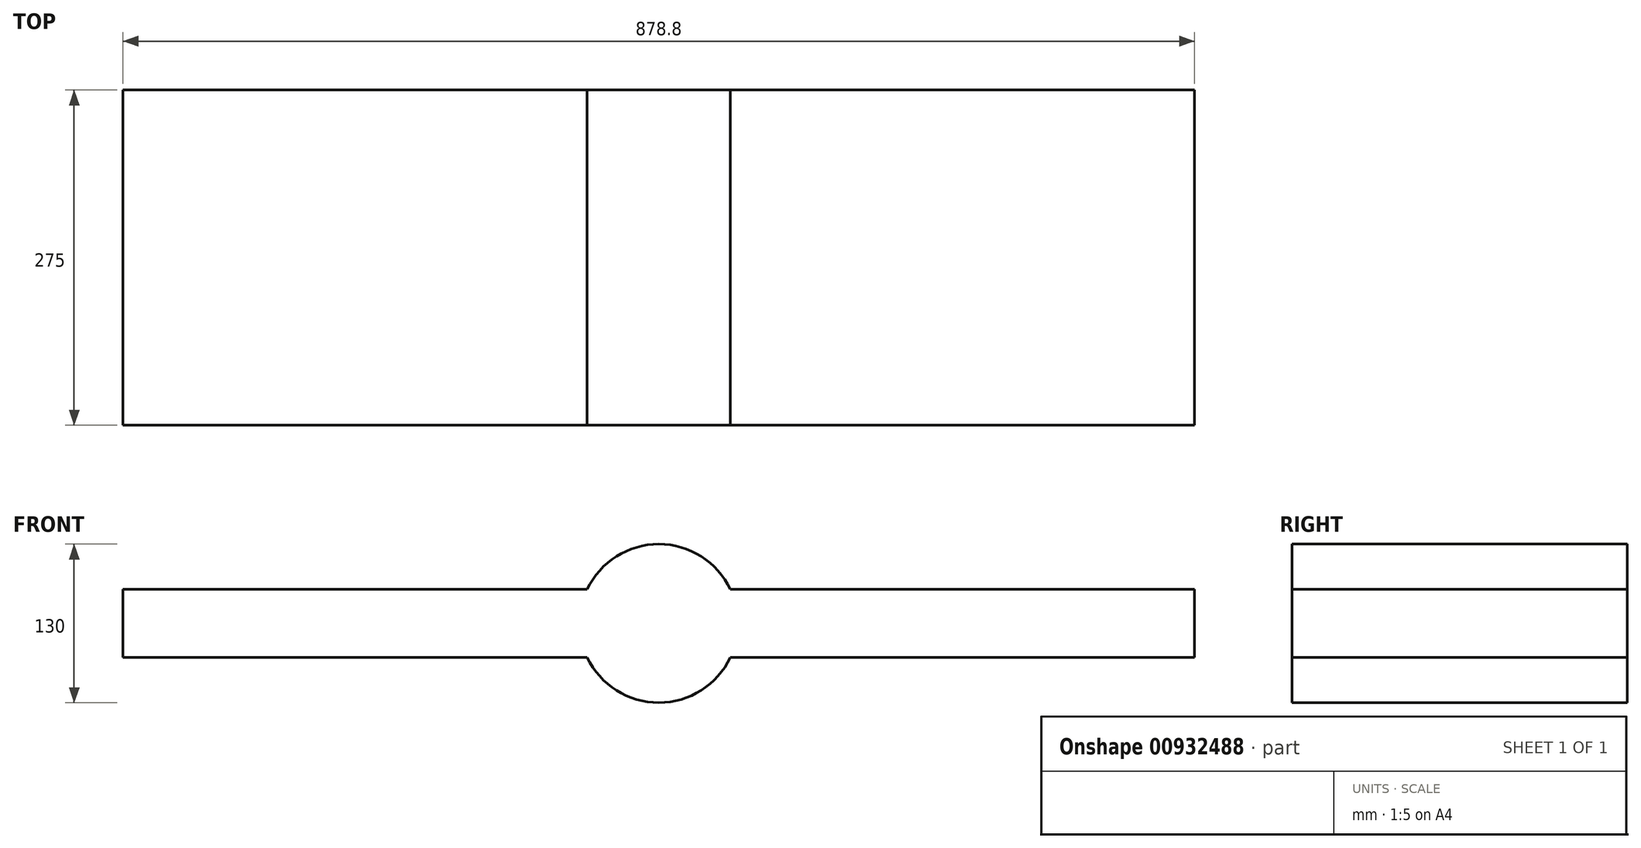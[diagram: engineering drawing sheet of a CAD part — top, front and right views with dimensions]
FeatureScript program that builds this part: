
annotation { "Feature Type Name" : "Feature", "Feature Type Description" : "" }
export const myFeature = defineFeature(function(context is Context, id is Id, definition is map)
    precondition{}
    {
        {
            var Q0;
            Q0=qCreatedBy(makeId("Front.planeOp"),FACE);
            var sketch = newSketch(context, id + "F0", { "sketchPlane" : qUnion([Q0])});
            skCircle(sketch, "E0", {"center": v(0, 0) * mm, "radius": 65 * mm});
            skLineSegment(sketch, "E1", {"start": v(0, 0) * mm, "end": v(-65, 0) * mm});
            skLineSegment(sketch, "E2", {"start": v(0, 65) * mm, "end": v(0, 0) * mm});
            skLineSegment(sketch, "E3", {"start": v(65, 0) * mm, "end": v(0, 0) * mm});
            skLineSegment(sketch, "E4", {"start": v(0, -65) * mm, "end": v(0, 0) * mm});
            skLineSegment(sketch, "E5.bottom", {"start": v(439.4, 27.92) * mm, "end": v(-439.4, 27.92) * mm});
            skLineSegment(sketch, "E5.top", {"start": v(439.4, -27.92) * mm, "end": v(-439.4, -27.92) * mm});
            skLineSegment(sketch, "E5.left", {"start": v(439.4, 27.92) * mm, "end": v(439.4, -27.92) * mm});
            skLineSegment(sketch, "E5.right", {"start": v(-439.4, 27.92) * mm, "end": v(-439.4, -27.92) * mm});
            skSolve(sketch);
        }
        {
            var Q0;
            {var subQ0=sQuery(id+"F0.wireOp",EDGE,"E5.right");Q0=makeQuery(id+"F0.imprint","IMPRINT",FACE,{"disambiguationData":[TD([[makeQuery(id+"F0.imprint","IMPRINT",EDGE,{"derivedFrom":subQ0}),1.0]])]});}
            var Q1;
            {var subQ0=sQuery(id+"F0.wireOp",EDGE,"E5.left");Q1=makeQuery(id+"F0.imprint","IMPRINT",FACE,{"disambiguationData":[TD([[makeQuery(id+"F0.imprint","IMPRINT",EDGE,{"derivedFrom":subQ0}),-1.0]])]});}
            var Q2;
            {var subQ0=sQuery(id+"F0.wireOp",EDGE,"E1");Q2=makeQuery(id+"F0.imprint","IMPRINT",FACE,{"disambiguationData":[TD([[makeQuery(id+"F0.imprint","IMPRINT",EDGE,{"derivedFrom":subQ0}),-1.0]])]});}
            var Q3;
            {var subQ0=sQuery(id+"F0.wireOp",EDGE,"E3");Q3=makeQuery(id+"F0.imprint","IMPRINT",FACE,{"disambiguationData":[TD([[makeQuery(id+"F0.imprint","IMPRINT",EDGE,{"derivedFrom":subQ0}),-1.0]])]});}
            var Q4;
            {var subQ0=sQuery(id+"F0.wireOp",EDGE,"E2");var subQ1=sQuery(id+"F0.wireOp",EDGE,"E0");var subQ2=makeQuery(id+"F0.imprint","INTERSECT",VERTEX,{"derivedFrom":[subQ1,subQ0]});Q4=makeQuery(id+"F0.imprint","IMPRINT",FACE,{"disambiguationData":[TD([[makeQuery(id+"F0.imprint","IMPRINT",EDGE,{"disambiguationData":[TD([[subQ2,-1.0]])],"derivedFrom":subQ1}),1.0]])]});}
            var Q5;
            {var subQ0=sQuery(id+"F0.wireOp",EDGE,"E4");var subQ1=sQuery(id+"F0.wireOp",EDGE,"E0");var subQ2=makeQuery(id+"F0.imprint","INTERSECT",VERTEX,{"derivedFrom":[subQ1,subQ0]});Q5=makeQuery(id+"F0.imprint","IMPRINT",FACE,{"disambiguationData":[TD([[makeQuery(id+"F0.imprint","IMPRINT",EDGE,{"disambiguationData":[TD([[subQ2,1.0]])],"derivedFrom":subQ1}),1.0]])]});}
            var Q6;
            {var subQ0=sQuery(id+"F0.wireOp",EDGE,"E1");Q6=makeQuery(id+"F0.imprint","IMPRINT",FACE,{"disambiguationData":[TD([[makeQuery(id+"F0.imprint","IMPRINT",EDGE,{"derivedFrom":subQ0}),1.0]])]});}
            var Q7;
            {var subQ0=sQuery(id+"F0.wireOp",EDGE,"E3");Q7=makeQuery(id+"F0.imprint","IMPRINT",FACE,{"disambiguationData":[TD([[makeQuery(id+"F0.imprint","IMPRINT",EDGE,{"derivedFrom":subQ0}),1.0]])]});}
            var Q8;
            {var subQ0=sQuery(id+"F0.wireOp",EDGE,"E4");var subQ1=sQuery(id+"F0.wireOp",EDGE,"E0");var subQ2=makeQuery(id+"F0.imprint","INTERSECT",VERTEX,{"derivedFrom":[subQ1,subQ0]});Q8=makeQuery(id+"F0.imprint","IMPRINT",FACE,{"disambiguationData":[TD([[makeQuery(id+"F0.imprint","IMPRINT",EDGE,{"disambiguationData":[TD([[subQ2,-1.0]])],"derivedFrom":subQ1}),1.0]])]});}
            var Q9;
            {var subQ0=sQuery(id+"F0.wireOp",EDGE,"E2");var subQ1=sQuery(id+"F0.wireOp",EDGE,"E0");var subQ2=makeQuery(id+"F0.imprint","INTERSECT",VERTEX,{"derivedFrom":[subQ1,subQ0]});Q9=makeQuery(id+"F0.imprint","IMPRINT",FACE,{"disambiguationData":[TD([[makeQuery(id+"F0.imprint","IMPRINT",EDGE,{"disambiguationData":[TD([[subQ2,1.0]])],"derivedFrom":subQ1}),1.0]])]});}
            extrude(context, id + "F1", {"entities" : qUnion([Q0, Q1, Q2, Q3, Q4, Q5, Q6, Q7, Q8, Q9]), "oppositeDirection" : true, "depth" : 275 * mm, "offsetDistance" : 25 * mm});
        }
    });
